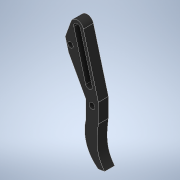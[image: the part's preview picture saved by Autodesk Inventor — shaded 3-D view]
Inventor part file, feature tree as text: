
AUTODESK INVENTOR PART (.ipt)
format: ipt  version: 2021 (Build 250183000, 183)  size: 168,960 bytes
history: native  units: mm
features: extrude x1, sketch x1
ambient origin geometry x8: Origin, YZ Plane, XZ Plane, XY Plane, X Axis, Y Axis, Z Axis, Center Point
bodies: Solid1 (feature_tree)
feature tree (2):
  extrude  "Extrusion1"  Depth=3.0mm
  sketch  "Sketch1"  dims[d5=4.8mm d6=0.0mm d8=1.0mm d9=3.0mm d10=3.0mm d11=18.0mm d12=8.0mm d13=5.0mm d15=0.5mm d17=1.0mm d18=4.0mm d19=8.0mm d25=6.0mm d26=3.0mm d27=9.0mm d61=3.2mm d62=27.5mm d63=5.0mm d64=2.8mm d65=3.0mm d68=6.0mm d69=1.8mm d70=2.5mm d72=4.0mm d73=15.0deg d74=15.0mm d75=3.5mm d76=1.5mm]
